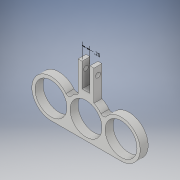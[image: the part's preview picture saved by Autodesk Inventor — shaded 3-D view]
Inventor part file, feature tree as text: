
AUTODESK INVENTOR PART (.ipt)
format: ipt  version: 2018 (Build 220112000, 112)  size: 160,256 bytes
history: native  units: in
note: dims shown in document units (in); Inventor stores cm internally (conversion verified against a paired STEP export)
features: extrude x3, sketch x3, other x2, fillet x1
ambient origin geometry x8: Origin, YZ Plane, XZ Plane, XY Plane, X Axis, Y Axis, Z Axis, Center Point
bodies: Solid1 (feature_tree)
feature tree (9):
  other  "Annotations"
  extrude  "Extrusion1"  Depth=0.0787in
  extrude  "Extrusion3"  Depth=0.3937in
  fillet  "Fillet2"  Radius=0.0984in
  extrude  "Extrusion4"  Depth=0.1969in TaperAngle=0.0deg
  sketch  "Sketch1"  dims[d1=0.6299in d4=0.0787in]
  sketch  "Sketch3"  dims[d12=0.0984in d13=0.3937in d14=0.0984in]
  sketch  "Sketch4"  dims[d15=0.5906in d16=0.1969in d17=0.0in d23=0.9449in d24=0.7874in d26=0.7874in d27=0.1969in d28=0.0in d29=0.1969in d30=0.1969in d31=0.1181in d32=0.3937in d33=0.0in d36=0.0787in d44=0.1969in d41=0.2956in d42=0.1041in d43=0.1969in]
  other  "Linear Dimension 1"
